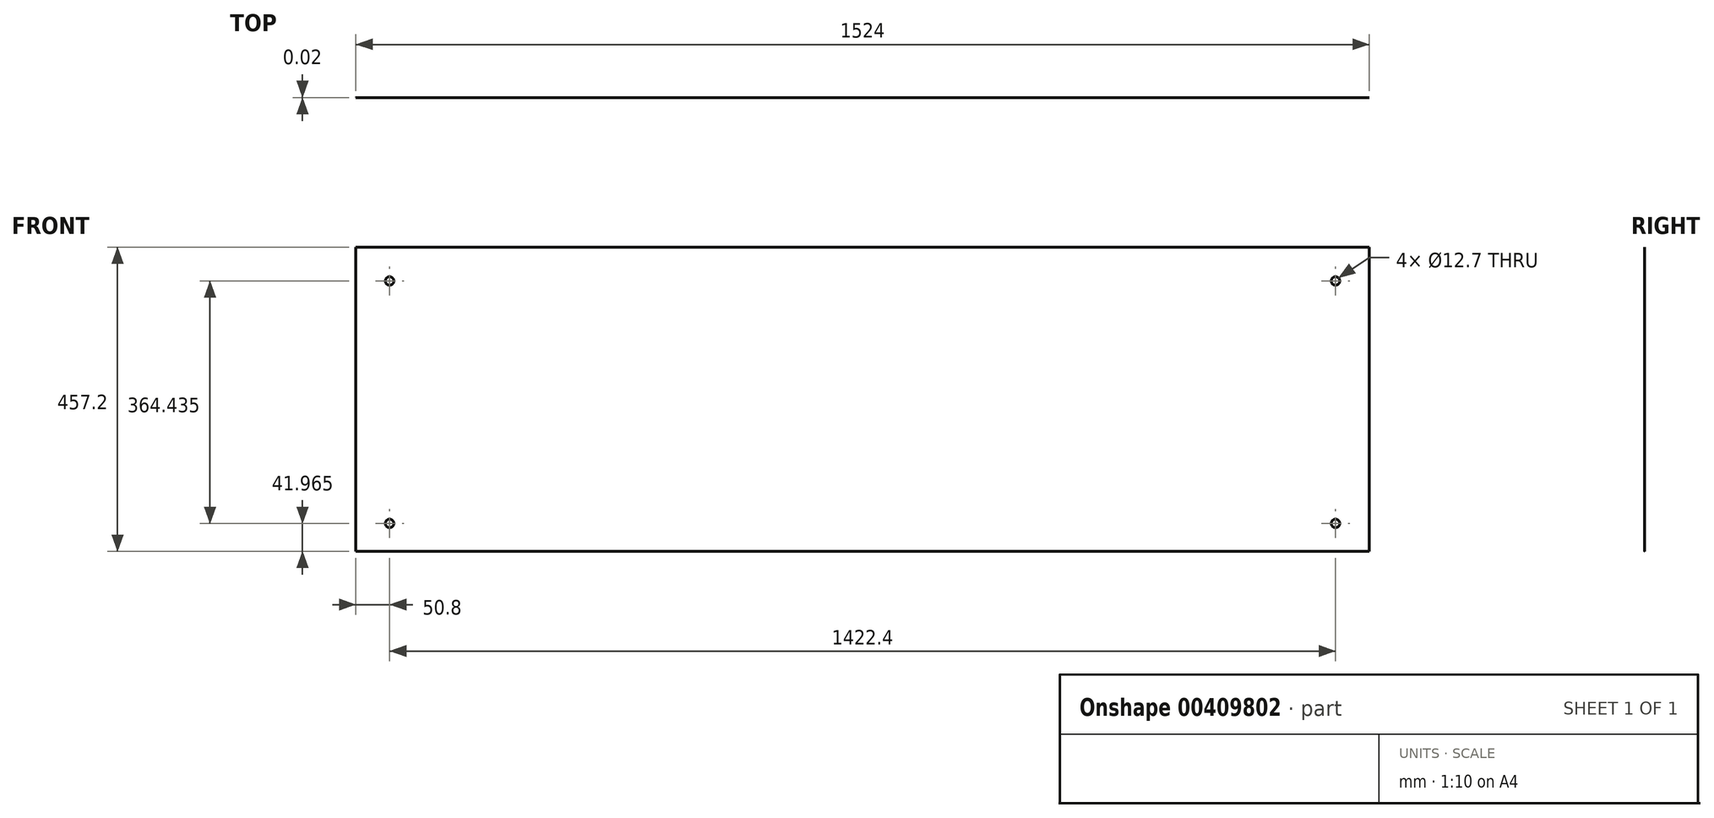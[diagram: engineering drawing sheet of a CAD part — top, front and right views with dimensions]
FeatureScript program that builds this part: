
annotation { "Feature Type Name" : "Feature", "Feature Type Description" : "" }
export const myFeature = defineFeature(function(context is Context, id is Id, definition is map)
    precondition{}
    {
        {
            var Q0;
            Q0=qCreatedBy(makeId("Front.planeOp"),FACE);
            var sketch = newSketch(context, id + "F0", { "sketchPlane" : qUnion([Q0])});
            skLineSegment(sketch, "E0.bottom", {"start": v(-762, 228.6) * mm, "end": v(762, 228.6) * mm});
            skLineSegment(sketch, "E0.top", {"start": v(-762, -228.6) * mm, "end": v(762, -228.6) * mm});
            skLineSegment(sketch, "E0.left", {"start": v(-762, 228.6) * mm, "end": v(-762, -228.6) * mm});
            skLineSegment(sketch, "E0.right", {"start": v(762, 228.6) * mm, "end": v(762, -228.6) * mm});
            skPoint(sketch, "E0.middle", {"position": v(0, 0) * mm});
            skSolve(sketch);
        }
        {
            var Q0;
            Q0=makeQuery(id+"F0.imprint","IMPRINT",FACE,{"disambiguationData":[TD([[makeQuery(id+"F0.imprint","IMPRINT",EDGE,{"derivedFrom":sQuery(id+"F0.wireOp",EDGE,"E0.bottom")}),-1.0]])]});
            extrude(context, id + "F1", {"entities" : qUnion([Q0]), "depth" : 5 / 203.2 * mm});
        }
        {
            var Q0;
            Q0=makeQuery(id+"F1.opExtrude","CAP_FACE",FACE,{"disambiguationData":[OSD([sQuery(id+"F0.wireOp",EDGE,"E0.bottom"),sQuery(id+"F0.wireOp",EDGE,"E0.top"),sQuery(id+"F0.wireOp",EDGE,"E0.left"),sQuery(id+"F0.wireOp",EDGE,"E0.right")])],"isStart":false});
            fillet(context, id + "F2", {"entities" : qUnion([Q0]), "radius" : 12.7 * mm, "tangentPropagation" : true, "allowEdgeOverflow" : false});
        }
        {
            var Q0;
            Q0=makeQuery(id+"F1.opExtrude","CAP_FACE",FACE,{"disambiguationData":[OSD([sQuery(id+"F0.wireOp",EDGE,"E0.bottom"),sQuery(id+"F0.wireOp",EDGE,"E0.top"),sQuery(id+"F0.wireOp",EDGE,"E0.left"),sQuery(id+"F0.wireOp",EDGE,"E0.right")])],"isStart":true});
            var sketch = newSketch(context, id + "F3", { "sketchPlane" : qUnion([Q0])});
            skPoint(sketch, "E1", {"position": v(-711.2, 177.8) * mm});
            skPoint(sketch, "E2", {"position": v(711.2, 177.8) * mm});
            skPoint(sketch, "E3", {"position": v(711.2, -186.63) * mm});
            skPoint(sketch, "E4", {"position": v(-711.2, -186.63) * mm});
            skCircle(sketch, "E5", {"center": v(711.2, 177.8) * mm, "radius": 10.97 * mm});
            skSolve(sketch);
        }
        {
            var Q0;
            Q0=sQuery(id+"F3.wireOp",VERTEX,"E1");
            var Q1;
            Q1=sQuery(id+"F3.wireOp",VERTEX,"E4");
            var Q2;
            Q2=sQuery(id+"F3.wireOp",VERTEX,"E3");
            var Q3;
            Q3=sQuery(id+"F3.wireOp",VERTEX,"E2");
            var Q4;
            Q4=makeQuery(id+"F1.opExtrude","SWEPT_BODY",BODY,{"disambiguationData":[OSD([sQuery(id+"F0.wireOp",EDGE,"E0.bottom"),sQuery(id+"F0.wireOp",EDGE,"E0.top"),sQuery(id+"F0.wireOp",EDGE,"E0.left"),sQuery(id+"F0.wireOp",EDGE,"E0.right")])]});
            hole(context, id + "F4", {"style" : HoleStyle.SIMPLE, "endStyle" : HoleEndStyle.BLIND, "holeDiameter" : 12.7 * mm, "holeDepth" : 9.52 * mm, "isTappedThrough" : true, "tappedDepth" : 12.7 * mm, "tapClearance" : 3, "locations" : qUnion([Q0, Q1, Q2, Q3]), "scope" : qUnion([Q4])});
        }
    });
